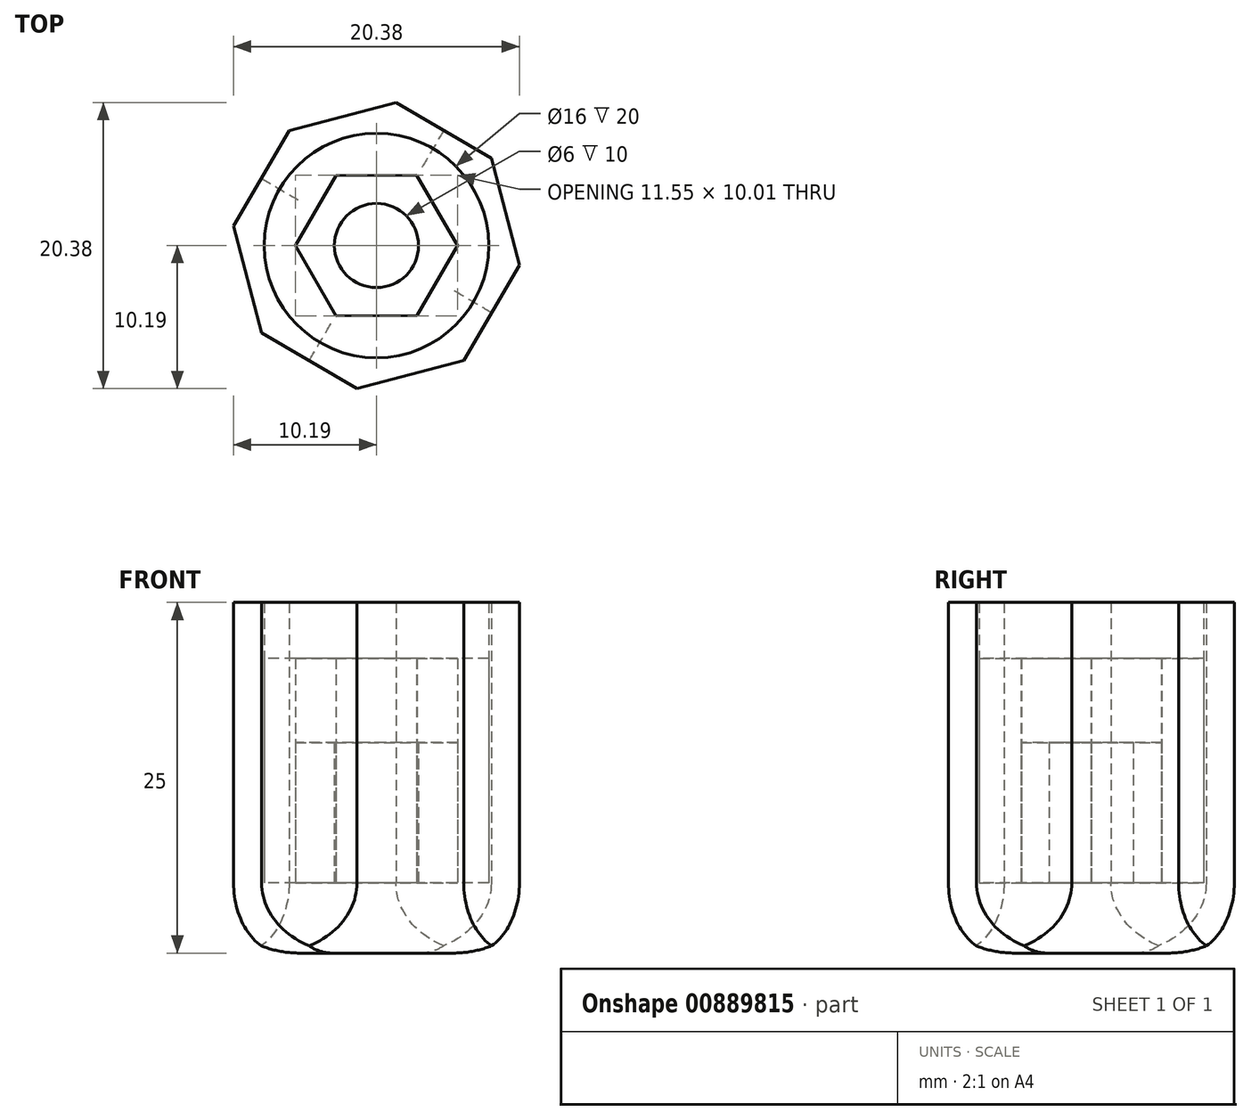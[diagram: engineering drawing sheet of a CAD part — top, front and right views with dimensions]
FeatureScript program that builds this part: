
annotation { "Feature Type Name" : "Feature", "Feature Type Description" : "" }
export const myFeature = defineFeature(function(context is Context, id is Id, definition is map)
    precondition{}
    {
        {
            var Q0;
            Q0=qCreatedBy(makeId("Top.planeOp"),FACE);
            var sketch = newSketch(context, id + "F0", { "sketchPlane" : qUnion([Q0])});
            skCircle(sketch, "E0.cCircle", {"center": v(0, 0) * mm, "radius": 5 * mm, "construction": true});
            skLineSegment(sketch, "E0.0", {"start": v(2.88, 5) * mm, "end": v(5.77, 0.01) * mm});
            skLineSegment(sketch, "E0.1", {"start": v(5.77, 0.01) * mm, "end": v(2.9, -5) * mm});
            skLineSegment(sketch, "E0.2", {"start": v(2.9, -5) * mm, "end": v(-2.88, -5) * mm});
            skLineSegment(sketch, "E0.3", {"start": v(-2.88, -5) * mm, "end": v(-5.77, -0.01) * mm});
            skLineSegment(sketch, "E0.4", {"start": v(-5.77, -0.01) * mm, "end": v(-2.9, 5) * mm});
            skLineSegment(sketch, "E0.5", {"start": v(-2.9, 5) * mm, "end": v(2.88, 5) * mm});
            skPoint(sketch, "E0.0.midPoint", {"position": v(4.32, 2.51) * mm});
            skCircle(sketch, "E1.cCircle", {"center": v(0, 0) * mm, "radius": 9.5 * mm, "construction": true});
            skLineSegment(sketch, "E1.0", {"start": v(10.19, -1.39) * mm, "end": v(6.22, -8.19) * mm});
            skLineSegment(sketch, "E1.1", {"start": v(6.22, -8.19) * mm, "end": v(-1.39, -10.19) * mm});
            skLineSegment(sketch, "E1.2", {"start": v(-1.39, -10.19) * mm, "end": v(-8.19, -6.22) * mm});
            skLineSegment(sketch, "E1.3", {"start": v(-8.19, -6.22) * mm, "end": v(-10.19, 1.39) * mm});
            skLineSegment(sketch, "E1.4", {"start": v(-10.19, 1.39) * mm, "end": v(-6.22, 8.19) * mm});
            skLineSegment(sketch, "E1.5", {"start": v(-6.22, 8.19) * mm, "end": v(1.39, 10.19) * mm});
            skLineSegment(sketch, "E1.6", {"start": v(1.39, 10.19) * mm, "end": v(8.19, 6.22) * mm});
            skLineSegment(sketch, "E1.7", {"start": v(8.19, 6.22) * mm, "end": v(10.19, -1.39) * mm});
            skPoint(sketch, "E1.0.midPoint", {"position": v(8.2, -4.79) * mm});
            skCircle(sketch, "E2", {"center": v(0, 0) * mm, "radius": 3 * mm});
            skCircle(sketch, "E3", {"center": v(0, 0) * mm, "radius": 8 * mm});
            skSolve(sketch);
        }
        {
            var Q0;
            Q0=makeQuery(id+"F0.imprint","IMPRINT",FACE,{"disambiguationData":[TD([[makeQuery(id+"F0.imprint","IMPRINT",EDGE,{"derivedFrom":sQuery(id+"F0.wireOp",EDGE,"E1.0")}),-1.0]])]});
            extrude(context, id + "F1", {"entities" : qUnion([Q0]), "depth" : 20 * mm, "offsetDistance" : 25 * mm});
        }
        {
            var Q0;
            Q0=makeQuery(id+"F0.imprint","IMPRINT",FACE,{"disambiguationData":[TD([[makeQuery(id+"F0.imprint","IMPRINT",EDGE,{"derivedFrom":sQuery(id+"F0.wireOp",EDGE,"E0.0")}),-1.0]])]});
            var Q1;
            Q1=makeQuery(id+"F0.imprint","IMPRINT",FACE,{"disambiguationData":[TD([[makeQuery(id+"F0.imprint","IMPRINT",EDGE,{"derivedFrom":sQuery(id+"F0.wireOp",EDGE,"E2")}),1.0]])]});
            var Q2;
            Q2=makeQuery(id+"F0.imprint","IMPRINT",FACE,{"disambiguationData":[TD([[makeQuery(id+"F0.imprint","IMPRINT",EDGE,{"derivedFrom":sQuery(id+"F0.wireOp",EDGE,"E0.0")}),1.0]])]});
            var Q3;
            Q3=makeQuery(id+"F0.imprint","IMPRINT",FACE,{"disambiguationData":[TD([[makeQuery(id+"F0.imprint","IMPRINT",EDGE,{"derivedFrom":sQuery(id+"F0.wireOp",EDGE,"E1.0")}),-1.0]])]});
            extrude(context, id + "F2", {"entities" : qUnion([Q0, Q1, Q2, Q3]), "operationType" : NewBodyOperationType.ADD, "depth" : -5 * mm, "offsetDistance" : 25 * mm});
        }
        {
            var Q0;
            Q0=makeQuery(id+"F0.imprint","IMPRINT",FACE,{"disambiguationData":[TD([[makeQuery(id+"F0.imprint","IMPRINT",EDGE,{"derivedFrom":sQuery(id+"F0.wireOp",EDGE,"E0.0")}),-1.0]])]});
            extrude(context, id + "F3", {"entities" : qUnion([Q0]), "operationType" : NewBodyOperationType.ADD, "depth" : 10 * mm, "offsetDistance" : 25 * mm});
        }
        {
            var Q0;
            Q0=makeQuery(id+"F0.imprint","IMPRINT",FACE,{"disambiguationData":[TD([[makeQuery(id+"F0.imprint","IMPRINT",EDGE,{"derivedFrom":sQuery(id+"F0.wireOp",EDGE,"E0.0")}),1.0]])]});
            extrude(context, id + "F4", {"entities" : qUnion([Q0]), "depth" : 16 * mm, "offsetDistance" : 25 * mm});
        }
        {
            var Q0;
            Q0=makeQuery(id+"F2.opExtrude","CAP_EDGE",EDGE,{"disambiguationData":[OSD([sQuery(id+"F0.wireOp",EDGE,"E1.1")])],"isStart":false});
            var Q1;
            Q1=makeQuery(id+"F2.opExtrude","CAP_EDGE",EDGE,{"disambiguationData":[OSD([sQuery(id+"F0.wireOp",EDGE,"E1.3")])],"isStart":false});
            var Q2;
            Q2=makeQuery(id+"F2.opExtrude","CAP_EDGE",EDGE,{"disambiguationData":[OSD([sQuery(id+"F0.wireOp",EDGE,"E1.5")])],"isStart":false});
            var Q3;
            Q3=makeQuery(id+"F2.opExtrude","CAP_EDGE",EDGE,{"disambiguationData":[OSD([sQuery(id+"F0.wireOp",EDGE,"E1.7")])],"isStart":false});
            fillet(context, id + "F5", {"entities" : qUnion([Q0, Q1, Q2, Q3]), "radius" : 5 * mm, "tangentPropagation" : true, "allowEdgeOverflow" : false});
        }
    });
